# Revit family: SANINDUSA_129330004_NewWCcare_76x52NewWCcareWashbasinwithIntegratedHandle76x52_V0
name_source: partatom
category: Plumbing Fixtures
units: mm (PartAtom-declared; Revit-internal decimal feet)

## family parameters
Cut with Voids When Loaded = No
Host = Face
Part Type = Normal
Room Calculation Point = No
Round Connector Dimension = Use Diameter
Shared = No

## types (1)
- SANINDUSA_129330004_NewWCcare_76x52NewWCcareWashbasinwithIntegratedHandle76x52_V0
    AssetType = Fixed
    CodePerformance = EN 14688:2006  CL 20
    Color = white
    Constituents = 48011U-chromed embellishment ring (included), 42902-Pneumatic fixation for washbasin 65 New Wccare (not included), 4V9211-Universal tic tac pop up waste(not included) , 4V9411-Universal tic tac pop up waste with little ABS mirror(not included) , 4V9111-Universal tic tac pop up waste with big round mirror(not included)
    Default Elevation = 1219 mm
    Description = Waste water appliance for washing the upper parts of the body.
    DrainSize = 47 mm  [stored 0.154199 ft]
    Element Type = WASHHANDBASIN: Waste water appliance for washing the upper parts of the body.
    Features = "Installation wall-mounted. Glazed on all sides. Not rectified. Ergonomic shape adapted to the handicapped.
Front cutout for an easy approach to the basin. 
Armrest on upper surface.
Wide side flaps for safe and comfortable armrest. 
Shape of the side edges for easy grip, helping the user's movement.
Reduced height of the basin that allows the approach to the washbasin of persons in wheelchairs."
    Finish = gloss
    Installation Instructions = https://www.tec.sanindusa.pt
    Manufacturer = Sanindusa
    ManufacturerName = Sanindusa
    ManufacturerURL = www.tec.sanindusa.pt
    Material = vitreous china
    Model = 129330004
    ModelNumber = 129330004
    ModelReference = New Wccare
    Name = 76x52 New Wccare washbasin
    NominalDepth = 102 mm
    NominalHeight = 155 mm  [stored 0.50853 ft]
    NominalLength = 759 mm  [stored 2.49016 ft]
    NominalWidth = 522 mm
    Pre-defined type (IFC) = WASHHANDBASIN
    ProductInformation = https://www.tec.sanindusa.pt
    ProductionYear = 2014
    Size = 76x52
    SpilloverLevel = 53
    Type (IFC) = IfcSanitaryTerminalType
    URL = www.tec.sanindusa.pt
    Version = 1
    WarrantyDescription = https://www.tec.sanindusa.pt
    WarrantyDurationParts = 5
    WarrantyDurationUnit = year
    WashHandBasinMounting = wallhung
    WashHandBasinType = handrinse
    Waste Connection = Yes
    Weight = 19.80 kg

note: [stored X ft] marks values corroborated as IEEE doubles in the binary element streams (Revit-internal decimal feet)

## geometry (parser evidence)
native form markers: Sweep x6
no freeform markers — native parametric forms only
